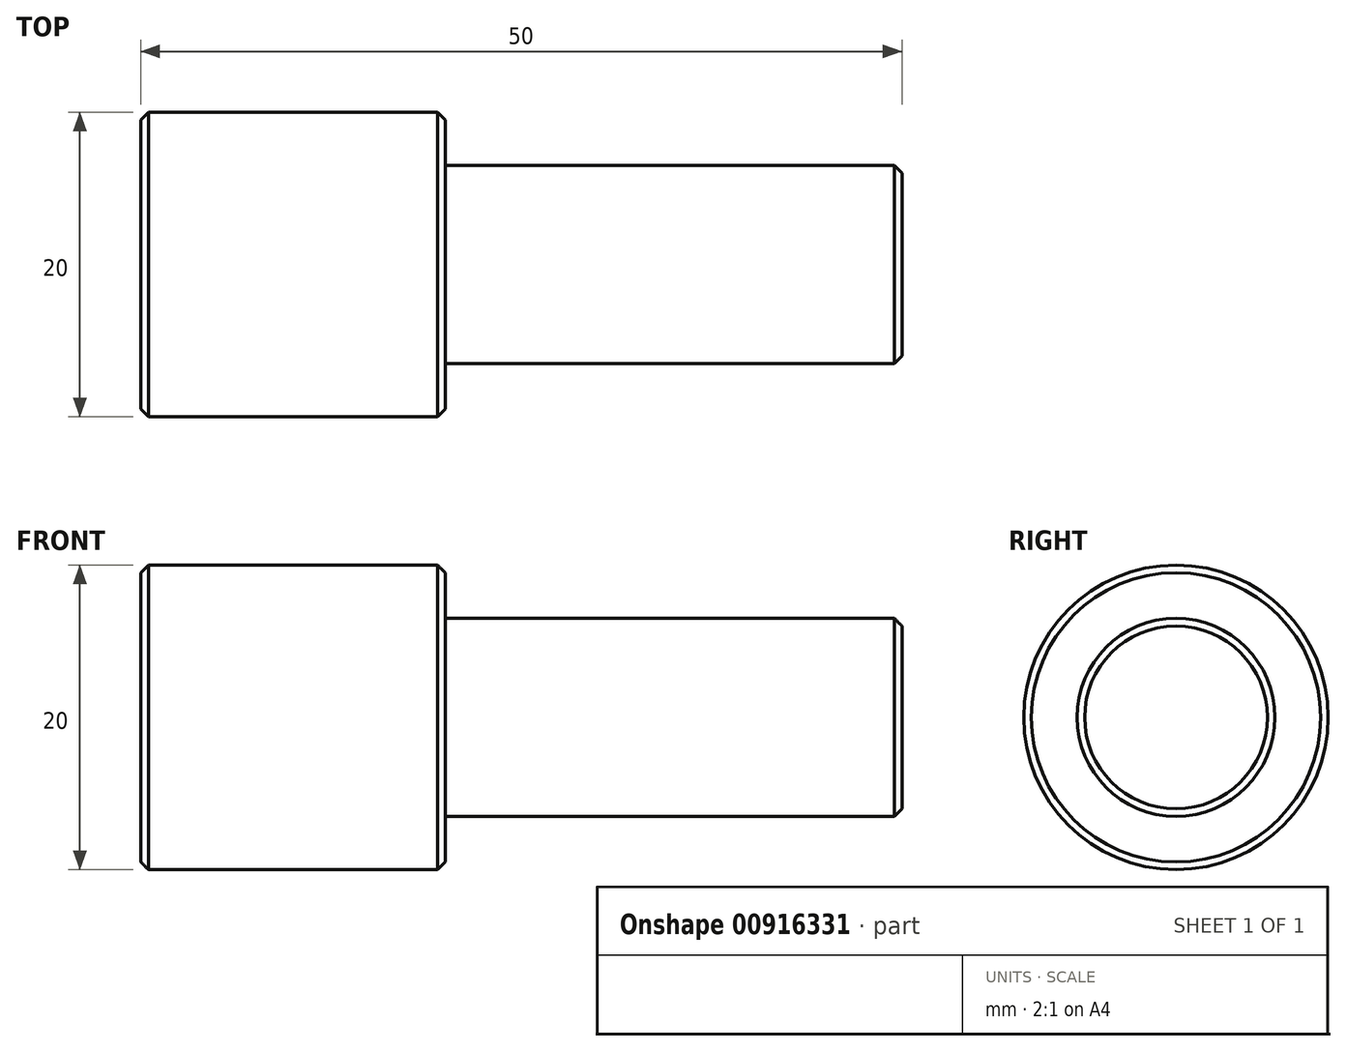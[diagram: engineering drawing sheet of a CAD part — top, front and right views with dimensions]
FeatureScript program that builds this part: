
annotation { "Feature Type Name" : "Feature", "Feature Type Description" : "" }
export const myFeature = defineFeature(function(context is Context, id is Id, definition is map)
    precondition{}
    {
        {
            var Q0;
            Q0=qCreatedBy(makeId("Front.planeOp"),FACE);
            var sketch = newSketch(context, id + "F0", { "sketchPlane" : qUnion([Q0])});
            skLineSegment(sketch, "E0", {"start": v(0, 0) * mm, "end": v(0, 3.5) * mm});
            skLineSegment(sketch, "E1", {"start": v(0, 3.5) * mm, "end": v(20, 3.5) * mm});
            skLineSegment(sketch, "E2", {"start": v(20, 3.5) * mm, "end": v(20, 0) * mm});
            skLineSegment(sketch, "E3", {"start": v(20, 0) * mm, "end": v(50, 0) * mm});
            skLineSegment(sketch, "E4", {"start": v(50, 0) * mm, "end": v(50, -6.5) * mm});
            skLineSegment(sketch, "E5", {"start": v(50, -6.5) * mm, "end": v(0, -6.5) * mm});
            skLineSegment(sketch, "E6", {"start": v(0, -6.5) * mm, "end": v(0, 0) * mm});
            skSolve(sketch);
        }
        {
            var Q0;
            Q0=makeQuery(id+"F0.imprint","IMPRINT",FACE,{"disambiguationData":[TD([[makeQuery(id+"F0.imprint","IMPRINT",EDGE,{"derivedFrom":sQuery(id+"F0.wireOp",EDGE,"E0")}),-1.0]])]});
            var Q1;
            Q1=sQuery(id+"F0.wireOp",EDGE,"E5");
            revolve(context, id + "F1", {"surfaceOperationType" : NewSurfaceOperationType.NEW, "entities" : qUnion([Q0]), "axis" : qUnion([Q1]), "revolveType" : RevolveType.FULL});
        }
        {
            var Q0;
            Q0=makeQuery(id+"F1.opRevolve","SWEPT_EDGE",EDGE,{"disambiguationData":[OSD([sQuery(id+"F0.wireOp",EDGE,"E3"),sQuery(id+"F0.wireOp",EDGE,"E4")])]});
            chamfer(context, id + "F2", {"entities" : qUnion([Q0]), "width" : 0.5 * mm, "tangentPropagation" : true});
        }
        {
            var Q0;
            Q0=makeQuery(id+"F1.opRevolve","SWEPT_EDGE",EDGE,{"disambiguationData":[OSD([sQuery(id+"F0.wireOp",EDGE,"E1"),sQuery(id+"F0.wireOp",EDGE,"E2")])]});
            var Q1;
            Q1=makeQuery(id+"F1.opRevolve","SWEPT_EDGE",EDGE,{"disambiguationData":[OSD([sQuery(id+"F0.wireOp",EDGE,"E0"),sQuery(id+"F0.wireOp",EDGE,"E1")])]});
            chamfer(context, id + "F3", {"entities" : qUnion([Q0, Q1]), "width" : 0.5 * mm, "tangentPropagation" : true});
        }
    });
